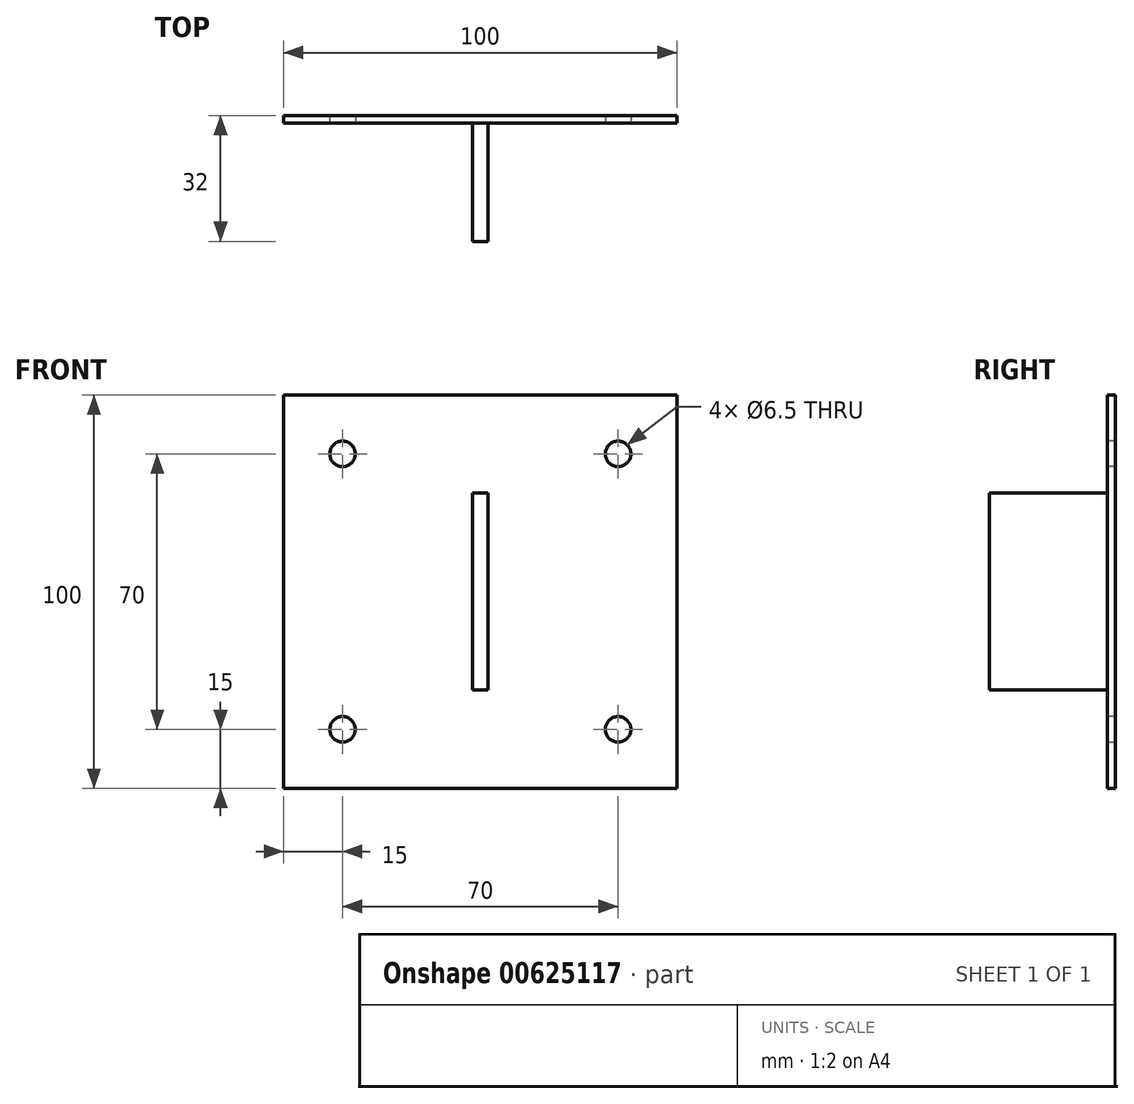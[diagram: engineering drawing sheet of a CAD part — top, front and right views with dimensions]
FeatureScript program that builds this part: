
annotation { "Feature Type Name" : "Feature", "Feature Type Description" : "" }
export const myFeature = defineFeature(function(context is Context, id is Id, definition is map)
    precondition{}
    {
        {
            var Q0;
            Q0=qCreatedBy(makeId("Front.planeOp"),FACE);
            var sketch = newSketch(context, id + "F0", { "sketchPlane" : qUnion([Q0])});
            skLineSegment(sketch, "E0.bottom", {"start": v(50, -50) * mm, "end": v(-50, -50) * mm});
            skLineSegment(sketch, "E0.top", {"start": v(50, 50) * mm, "end": v(-50, 50) * mm});
            skLineSegment(sketch, "E0.left", {"start": v(50, -50) * mm, "end": v(50, 50) * mm});
            skLineSegment(sketch, "E0.right", {"start": v(-50, -50) * mm, "end": v(-50, 50) * mm});
            skPoint(sketch, "E0.middle", {"position": v(0, 0) * mm});
            skSolve(sketch);
        }
        {
            var Q0;
            Q0 = qSketchRegion(id + "F0", true);
            extrude(context, id + "F1", {"entities" : qUnion([Q0]), "depth" : 2 * mm, "offsetDistance" : 25 * mm});
        }
        {
            var Q0;
            Q0=makeQuery(id+"F1.opExtrude","CAP_FACE",FACE,{"disambiguationData":[OSD([sQuery(id+"F0.wireOp",EDGE,"E0.bottom"),sQuery(id+"F0.wireOp",EDGE,"E0.top"),sQuery(id+"F0.wireOp",EDGE,"E0.left"),sQuery(id+"F0.wireOp",EDGE,"E0.right")])],"isStart":false});
            var sketch = newSketch(context, id + "F2", { "sketchPlane" : qUnion([Q0])});
            skLineSegment(sketch, "E1", {"start": v(0, 50) * mm, "end": v(0, -50) * mm, "construction": true});
            skLineSegment(sketch, "E2", {"start": v(-50, 0) * mm, "end": v(50, 0) * mm, "construction": true});
            skLineSegment(sketch, "E3", {"start": v(-50, 50) * mm, "end": v(-50, 35) * mm, "construction": true});
            skLineSegment(sketch, "E4", {"start": v(-50, 35) * mm, "end": v(-35, 35) * mm, "construction": true});
            skLineSegment(sketch, "E5", {"start": v(-50, -50) * mm, "end": v(-50, -35) * mm, "construction": true});
            skLineSegment(sketch, "E6", {"start": v(-50, -35) * mm, "end": v(-35, -35) * mm, "construction": true});
            skLineSegment(sketch, "E7", {"start": v(50, 50) * mm, "end": v(50, 35) * mm, "construction": true});
            skLineSegment(sketch, "E8", {"start": v(50, 35) * mm, "end": v(35, 35) * mm, "construction": true});
            skLineSegment(sketch, "E9", {"start": v(50, -50) * mm, "end": v(50, -35) * mm, "construction": true});
            skLineSegment(sketch, "E10", {"start": v(50, -35) * mm, "end": v(35, -35) * mm, "construction": true});
            skCircle(sketch, "E11", {"center": v(-35, 35) * mm, "radius": 3.25 * mm});
            skCircle(sketch, "E12", {"center": v(35, 35) * mm, "radius": 3.25 * mm});
            skCircle(sketch, "E13", {"center": v(35, -35) * mm, "radius": 3.25 * mm});
            skCircle(sketch, "E14", {"center": v(-35, -35) * mm, "radius": 3.25 * mm});
            skSolve(sketch);
        }
        {
            var Q0;
            Q0=makeQuery(id+"F2.imprint","IMPRINT",FACE,{"disambiguationData":[TD([[makeQuery(id+"F2.imprint","IMPRINT",EDGE,{"derivedFrom":sQuery(id+"F2.wireOp",EDGE,"E11")}),1.0]])]});
            var Q1;
            Q1=makeQuery(id+"F2.imprint","IMPRINT",FACE,{"disambiguationData":[TD([[makeQuery(id+"F2.imprint","IMPRINT",EDGE,{"derivedFrom":sQuery(id+"F2.wireOp",EDGE,"E12")}),1.0]])]});
            var Q2;
            Q2=makeQuery(id+"F2.imprint","IMPRINT",FACE,{"disambiguationData":[TD([[makeQuery(id+"F2.imprint","IMPRINT",EDGE,{"derivedFrom":sQuery(id+"F2.wireOp",EDGE,"E14")}),1.0]])]});
            var Q3;
            Q3=makeQuery(id+"F2.imprint","IMPRINT",FACE,{"disambiguationData":[TD([[makeQuery(id+"F2.imprint","IMPRINT",EDGE,{"derivedFrom":sQuery(id+"F2.wireOp",EDGE,"E13")}),1.0]])]});
            extrude(context, id + "F3", {"entities" : qUnion([Q0, Q1, Q2, Q3]), "operationType" : NewBodyOperationType.REMOVE, "endBound" : BoundingType.THROUGH_ALL, "oppositeDirection" : true, "depth" : 25 * mm, "offsetDistance" : 25 * mm});
        }
        {
            var Q0;
            Q0=makeQuery(id+"F1.opExtrude","CAP_FACE",FACE,{"disambiguationData":[OSD([sQuery(id+"F0.wireOp",EDGE,"E0.bottom"),sQuery(id+"F0.wireOp",EDGE,"E0.top"),sQuery(id+"F0.wireOp",EDGE,"E0.left"),sQuery(id+"F0.wireOp",EDGE,"E0.right")])],"isStart":false});
            var sketch = newSketch(context, id + "F4", { "sketchPlane" : qUnion([Q0])});
            skLineSegment(sketch, "E15.bottom", {"start": v(2, -25) * mm, "end": v(-2, -25) * mm});
            skLineSegment(sketch, "E15.top", {"start": v(2, 25) * mm, "end": v(-2, 25) * mm});
            skLineSegment(sketch, "E15.left", {"start": v(2, -25) * mm, "end": v(2, 25) * mm});
            skLineSegment(sketch, "E15.right", {"start": v(-2, -25) * mm, "end": v(-2, 25) * mm});
            skPoint(sketch, "E15.middle", {"position": v(0, 0) * mm});
            skSolve(sketch);
        }
        {
            var Q0;
            Q0=makeQuery(id+"F4.imprint","IMPRINT",FACE,{"disambiguationData":[TD([[makeQuery(id+"F4.imprint","IMPRINT",EDGE,{"derivedFrom":sQuery(id+"F4.wireOp",EDGE,"E15.bottom")}),-1.0]])]});
            extrude(context, id + "F5", {"entities" : qUnion([Q0]), "operationType" : NewBodyOperationType.ADD, "depth" : 30 * mm, "offsetDistance" : 25 * mm});
        }
    });
